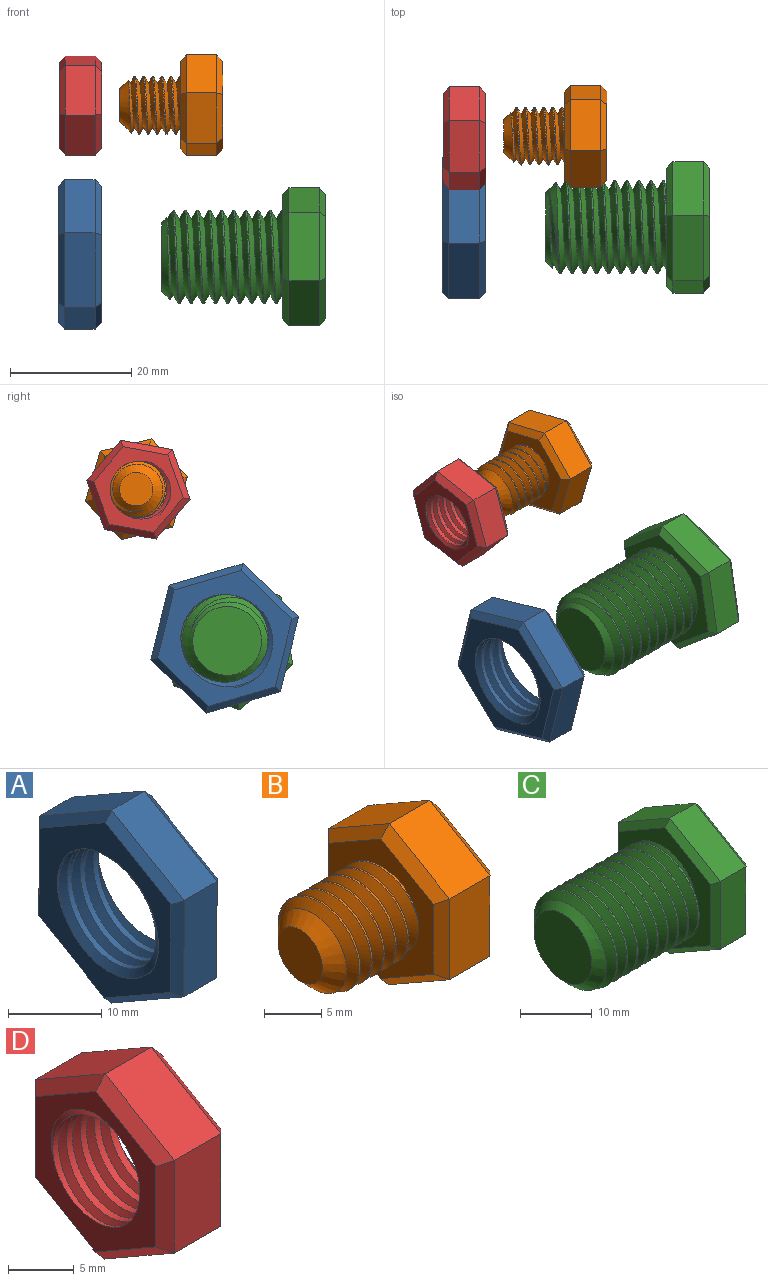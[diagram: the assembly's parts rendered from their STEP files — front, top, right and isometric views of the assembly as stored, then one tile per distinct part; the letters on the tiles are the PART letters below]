
ASSEMBLY  parts=4 mates=2
PART A: 23 faces, bbox 9.3x22.7x26 mm
  f0: cylinder r=7.24mm len=14.48mm, axis (1,0,0), area 111.6mm2, adj f7,f8,f21,f22
  f1: plane 10.98x6.38mm, normal (0,-0.5,0.86), area 63.5mm2, adj f2,f6,f14,f18
  f2: plane 12.7x5mm, normal (0,-1,0), area 63.5mm2, adj f1,f3,f12,f16
  f3: plane 11.02x6.32mm, normal (0,-0.5,-0.87), area 63.5mm2, adj f2,f4,f10,f15
  f4: plane 10.98x6.38mm, normal (0,0.5,-0.86), area 63.5mm2, adj f3,f5,f9,f17
  f5: plane 12.7x5mm, normal (0,1,0), area 63.5mm2, adj f4,f6,f11,f19
  f6: plane 11.02x6.32mm, normal (0,0.5,0.87), area 63.5mm2, adj f1,f5,f13,f20
  f7: plane 23.73x20.67mm, normal (-1,0,0), area 164.4mm2, adj f0,f9,f10,f11,f12,f13,f14,f21
  f8: plane 23.73x20.67mm, normal (1,0,0), area 164.4mm2, adj f0,f15,f16,f17,f18,f19,f20,f21
  f9: plane 10.99x6.96mm, normal (-0.71,0.36,-0.61), area 17.1mm2, adj f4,f7,f10,f11
  f10: plane 11.02x6.9mm, normal (-0.71,-0.35,-0.61), area 17.1mm2, adj f3,f7,f9,f12
  f11: plane 12.7x1.03mm, normal (-0.71,0.71,0), area 17.1mm2, adj f5,f7,f9,f13
  f12: plane 12.7x1.03mm, normal (-0.71,-0.71,0), area 17.1mm2, adj f2,f7,f10,f14
  f13: plane 11.02x6.9mm, normal (-0.71,0.35,0.61), area 17.1mm2, adj f6,f7,f11,f14
  f14: plane 10.99x6.96mm, normal (-0.71,-0.36,0.61), area 17.1mm2, adj f1,f7,f12,f13
  f15: plane 11.02x6.9mm, normal (0.71,-0.35,-0.61), area 17.1mm2, adj f3,f8,f16,f17
  f16: plane 12.7x1.03mm, normal (0.71,-0.71,0), area 17.1mm2, adj f2,f8,f15,f18
  f17: plane 10.99x6.96mm, normal (0.71,0.36,-0.61), area 17.1mm2, adj f4,f8,f15,f19
  f18: plane 10.99x6.96mm, normal (0.71,-0.36,0.61), area 17.1mm2, adj f1,f8,f16,f20
  f19: plane 12.7x1.03mm, normal (0.71,0.71,0), area 17.1mm2, adj f5,f8,f17,f20
  f20: plane 11.02x6.9mm, normal (0.71,0.35,0.61), area 17.1mm2, adj f6,f8,f18,f19
  f21: bspline ~19.31x16.73mm, area 223mm2, adj f0,f7,f8,f22
  f22: bspline ~19.31x16.73mm, area 223mm2, adj f0,f7,f8,f21
PART B: 25 faces, bbox 17.8x15.9x18.1 mm
  f0: cylinder r=4.75mm len=9.5mm, axis (1,0,0), area 28.1mm2, adj f1,f2,f4,f12
  f1: bspline ~10.97x9.91mm, area 196.7mm2, adj f0,f2,f4,f12
  f2: bspline ~10.97x10.66mm, area 196.6mm2, adj f0,f1,f4,f12
  f3: plane 5.5x5.5mm, normal (-1,0,0), area 23.8mm2, adj f4
  f4: cone r=4.75mm half-angle=45deg, axis (1,0,0), area 47.4mm2, adj f0,f1,f2,f3
  f5: plane 7.48x5mm, normal (0,-0.5,0.86), area 43.3mm2, adj f6,f10,f18,f22
  f6: plane 8.66x5mm, normal (0,-1,0), area 43.3mm2, adj f5,f7,f16,f20
  f7: plane 7.52x5mm, normal (0,-0.5,-0.87), area 43.3mm2, adj f6,f8,f14,f19
  f8: plane 7.48x5mm, normal (0,0.5,-0.86), area 43.3mm2, adj f7,f9,f13,f21
  f9: plane 8.66x5mm, normal (0,1,0), area 43.3mm2, adj f8,f10,f15,f23
  f10: plane 7.52x5mm, normal (0,0.5,0.87), area 43.3mm2, adj f5,f9,f17,f24
  f11: plane 15.01x13.03mm, normal (1,0,0), area 146.4mm2, adj f13,f14,f15,f16,f17,f18
  f12: plane 15.83x13.85mm, normal (-1,0,0), area 89.2mm2, adj f0,f1,f2,f19,f20,f21,f22,f23
  f13: plane 7.49x4.93mm, normal (0.71,0.36,-0.61), area 11.4mm2, adj f8,f11,f14,f15
  f14: plane 7.52x4.88mm, normal (0.71,-0.35,-0.61), area 11.4mm2, adj f7,f11,f13,f16
  f15: plane 8.66x1.03mm, normal (0.71,0.71,0), area 11.4mm2, adj f9,f11,f13,f17
  f16: plane 8.66x1.03mm, normal (0.71,-0.71,0), area 11.4mm2, adj f6,f11,f14,f18
  f17: plane 7.52x4.88mm, normal (0.71,0.35,0.61), area 11.4mm2, adj f10,f11,f15,f18
  f18: plane 7.49x4.93mm, normal (0.71,-0.36,0.61), area 11.4mm2, adj f5,f11,f16,f17
  f19: plane 7.52x4.88mm, normal (-0.71,-0.35,-0.61), area 11.4mm2, adj f7,f12,f20,f21
  f20: plane 8.66x1.03mm, normal (-0.71,-0.71,0), area 11.4mm2, adj f6,f12,f19,f22
  f21: plane 7.49x4.93mm, normal (-0.71,0.36,-0.61), area 11.4mm2, adj f8,f12,f19,f23
  f22: plane 7.49x4.93mm, normal (-0.71,-0.36,0.61), area 11.4mm2, adj f5,f12,f20,f24
  f23: plane 8.66x1.03mm, normal (-0.71,0.71,0), area 11.4mm2, adj f9,f12,f21,f24
  f24: plane 7.52x4.88mm, normal (-0.71,0.35,0.61), area 11.4mm2, adj f10,f12,f22,f23
PART C: 26 faces, bbox 27.7x20x23.1 mm
  f0: cylinder r=7.68mm len=18mm, axis (1,0,0), area 139.1mm2, adj f1,f2,f5,f13
  f1: bspline ~20.88x17.74mm, area 713.8mm2, adj f0,f2,f4,f5,f13
  f2: bspline ~21.88x17.74mm, area 715.1mm2, adj f0,f1,f4,f5,f13
  f3: plane 11.36x11.36mm, normal (-1,0,0), area 101.4mm2, adj f4
  f4: cone r=7.68mm half-angle=45deg, axis (1,0,0), area 63.2mm2, adj f1,f2,f3,f5
  f5: cone r=7.68mm half-angle=45deg, axis (1,0,0), area 13.2mm2, adj f0,f1,f2,f4
  f6: plane 9.98x5.81mm, normal (0,-0.5,0.86), area 57.7mm2, adj f7,f11,f19,f23
  f7: plane 11.55x5mm, normal (0,-1,0), area 57.7mm2, adj f6,f8,f17,f21
  f8: plane 10.02x5.74mm, normal (0,-0.5,-0.87), area 57.7mm2, adj f7,f9,f15,f20
  f9: plane 9.98x5.81mm, normal (0,0.5,-0.86), area 57.7mm2, adj f8,f10,f14,f22
  f10: plane 11.55x5mm, normal (0,1,0), area 57.7mm2, adj f9,f11,f16,f24
  f11: plane 10.02x5.74mm, normal (0,0.5,0.87), area 57.7mm2, adj f6,f10,f18,f25
  f12: plane 20.78x18.04mm, normal (1,0,0), area 280.6mm2, adj f14,f15,f16,f17,f18,f19
  f13: plane 20.78x18.04mm, normal (-1,0,0), area 125.2mm2, adj f0,f1,f2,f20,f21,f22,f23,f24
  f14: plane 9.98x6.38mm, normal (0.71,0.36,-0.61), area 15.5mm2, adj f9,f12,f15,f16
  f15: plane 10.02x6.32mm, normal (0.71,-0.35,-0.61), area 15.5mm2, adj f8,f12,f14,f17
  f16: plane 11.55x1.04mm, normal (0.71,0.71,0), area 15.5mm2, adj f10,f12,f14,f18
  f17: plane 11.55x1.04mm, normal (0.71,-0.71,0), area 15.5mm2, adj f7,f12,f15,f19
  f18: plane 10.02x6.32mm, normal (0.71,0.35,0.61), area 15.5mm2, adj f11,f12,f16,f19
  f19: plane 9.98x6.38mm, normal (0.71,-0.36,0.61), area 15.5mm2, adj f6,f12,f17,f18
  f20: plane 10.02x6.32mm, normal (-0.71,-0.35,-0.61), area 15.5mm2, adj f8,f13,f21,f22
  f21: plane 11.55x1.04mm, normal (-0.71,-0.71,0), area 15.5mm2, adj f7,f13,f20,f23
  f22: plane 9.98x6.38mm, normal (-0.71,0.36,-0.61), area 15.5mm2, adj f9,f13,f20,f24
  f23: plane 9.98x6.38mm, normal (-0.71,-0.36,0.61), area 15.5mm2, adj f6,f13,f21,f25
  f24: plane 11.55x1.04mm, normal (-0.71,0.71,0), area 15.5mm2, adj f10,f13,f22,f25
  f25: plane 10.02x6.32mm, normal (-0.71,0.35,0.61), area 15.5mm2, adj f11,f13,f23,f24
PART D: 23 faces, bbox 9.1x15.4x17.7 mm
  f0: plane 7.49x5mm, normal (0,-0.5,0.86), area 43.3mm2, adj f1,f5,f13,f17
  f1: plane 8.66x5mm, normal (0,-1,0), area 43.3mm2, adj f0,f2,f11,f15
  f2: plane 7.51x5mm, normal (0,-0.5,-0.87), area 43.3mm2, adj f1,f3,f9,f14
  f3: plane 7.49x5mm, normal (0,0.5,-0.86), area 43.3mm2, adj f2,f4,f8,f16
  f4: plane 8.66x5mm, normal (0,1,0), area 43.3mm2, adj f3,f5,f10,f18
  f5: plane 7.51x5mm, normal (0,0.5,0.87), area 43.3mm2, adj f0,f4,f12,f19
  f6: plane 15.37x13.38mm, normal (-1,0,0), area 71.4mm2, adj f8,f9,f10,f11,f12,f13,f20,f21
  f7: plane 15.37x13.38mm, normal (1,0,0), area 71.4mm2, adj f14,f15,f16,f17,f18,f19,f20,f21
  f8: plane 7.49x4.93mm, normal (-0.71,0.36,-0.61), area 11.4mm2, adj f3,f6,f9,f10
  f9: plane 7.51x4.89mm, normal (-0.71,-0.35,-0.61), area 11.4mm2, adj f2,f6,f8,f11
  f10: plane 8.66x1.02mm, normal (-0.71,0.71,0), area 11.4mm2, adj f4,f6,f8,f12
  f11: plane 8.66x1.02mm, normal (-0.71,-0.71,0), area 11.4mm2, adj f1,f6,f9,f13
  f12: plane 7.51x4.89mm, normal (-0.71,0.35,0.61), area 11.4mm2, adj f5,f6,f10,f13
  f13: plane 7.49x4.93mm, normal (-0.71,-0.36,0.61), area 11.4mm2, adj f0,f6,f11,f12
  f14: plane 7.51x4.89mm, normal (0.71,-0.35,-0.61), area 11.4mm2, adj f2,f7,f15,f16
  f15: plane 8.66x1.02mm, normal (0.71,-0.71,0), area 11.4mm2, adj f1,f7,f14,f17
  f16: plane 7.49x4.93mm, normal (0.71,0.36,-0.61), area 11.4mm2, adj f3,f7,f14,f18
  f17: plane 7.49x4.93mm, normal (0.71,-0.36,0.61), area 11.4mm2, adj f0,f7,f15,f19
  f18: plane 8.66x1.02mm, normal (0.71,0.71,0), area 11.4mm2, adj f4,f7,f16,f19
  f19: plane 7.51x4.89mm, normal (0.71,0.35,0.61), area 11.4mm2, adj f5,f7,f17,f18
  f20: cylinder r=4.66mm len=9.32mm, axis (1,0,0), area 85.4mm2, adj f6,f7,f21,f22
  f21: bspline ~12.5x10.82mm, area 128.4mm2, adj f6,f7,f20,f22
  f22: bspline ~12.5x10.82mm, area 128.5mm2, adj f6,f7,f20,f21
PLACE A rot(axis=(0,0.6,-0.8),180deg) t=(-55.27,-6.86,23.48)mm fixed
PLACE B rot(axis=(-1,0,0),43.8deg) t=(-31.66,7.73,48.08)mm
PLACE C rot(axis=(1,0,0),109.9deg) t=(-14.77,-7.25,23.06)mm
PLACE D rot(axis=(1,0,0),100.2deg) t=(-48.16,7.38,48.02)mm fixed
MATE cylindrical C.f0 <-> A.f7  axis (-1,0,0) through (-38.27,-7.25,23.06)mm
MATE cylindrical B.f0 <-> D.f6  axis (-1,0,0) through (-45.16,7.73,48.08)mm
